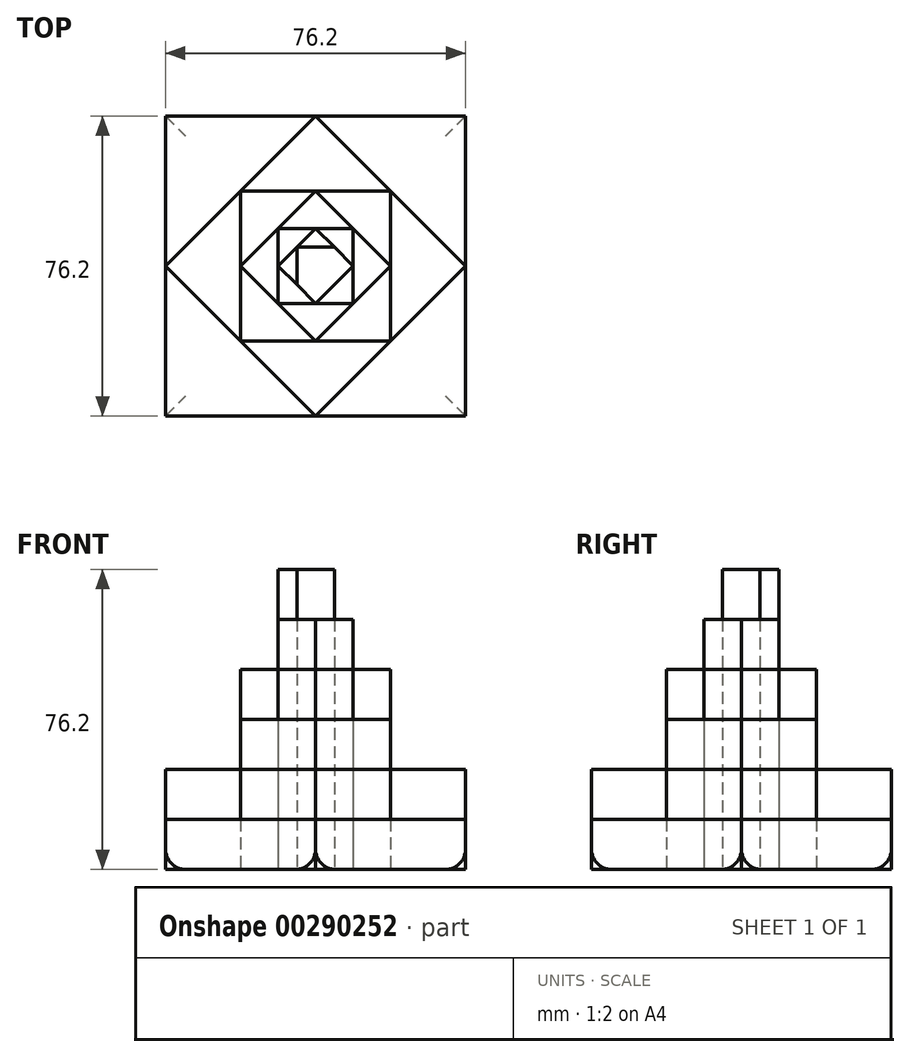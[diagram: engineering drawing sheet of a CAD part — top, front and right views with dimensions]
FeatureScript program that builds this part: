
annotation { "Feature Type Name" : "Feature", "Feature Type Description" : "" }
export const myFeature = defineFeature(function(context is Context, id is Id, definition is map)
    precondition{}
    {
        {
            var Q0;
            Q0=qCreatedBy(makeId("Top.planeOp"),FACE);
            var sketch = newSketch(context, id + "F0", { "sketchPlane" : qUnion([Q0])});
            skPoint(sketch, "E0", {"position": v(0, 0) * mm});
            skLineSegment(sketch, "E1", {"start": v(-38.1, 38.1) * mm, "end": v(-38.1, -38.1) * mm});
            skLineSegment(sketch, "E2", {"start": v(-38.1, -38.1) * mm, "end": v(38.1, -38.1) * mm});
            skLineSegment(sketch, "E3", {"start": v(38.1, -38.1) * mm, "end": v(38.1, 38.1) * mm});
            skLineSegment(sketch, "E4", {"start": v(-38.1, 38.1) * mm, "end": v(38.1, 38.1) * mm});
            skPoint(sketch, "E5", {"position": v(0, -38.1) * mm});
            skPoint(sketch, "E6", {"position": v(38.1, 0) * mm});
            skLineSegment(sketch, "E7", {"start": v(0, 38.1) * mm, "end": v(-38.1, 0) * mm});
            skLineSegment(sketch, "E8", {"start": v(-38.1, 0) * mm, "end": v(0, -38.1) * mm});
            skLineSegment(sketch, "E9", {"start": v(0, 38.1) * mm, "end": v(38.1, 0) * mm});
            skLineSegment(sketch, "E10", {"start": v(38.1, 0) * mm, "end": v(0, -38.1) * mm});
            skLineSegment(sketch, "E11", {"start": v(19.05, 19.05) * mm, "end": v(19.05, -19.05) * mm});
            skLineSegment(sketch, "E12", {"start": v(19.05, -19.05) * mm, "end": v(-19.05, -19.05) * mm});
            skLineSegment(sketch, "E13", {"start": v(-19.05, -19.05) * mm, "end": v(-19.05, 19.05) * mm});
            skLineSegment(sketch, "E14", {"start": v(-19.05, 19.05) * mm, "end": v(19.05, 19.05) * mm});
            skLineSegment(sketch, "E15", {"start": v(0, 19.05) * mm, "end": v(19.05, 0) * mm});
            skLineSegment(sketch, "E16", {"start": v(19.05, 0) * mm, "end": v(0, -19.05) * mm});
            skLineSegment(sketch, "E17", {"start": v(0, -19.05) * mm, "end": v(-19.05, 0) * mm});
            skLineSegment(sketch, "E18", {"start": v(-19.05, 0) * mm, "end": v(0, 19.05) * mm});
            skLineSegment(sketch, "E19", {"start": v(9.52, 9.52) * mm, "end": v(9.52, -9.53) * mm});
            skLineSegment(sketch, "E20", {"start": v(9.52, -9.53) * mm, "end": v(-9.53, -9.53) * mm});
            skLineSegment(sketch, "E21", {"start": v(-9.53, -9.53) * mm, "end": v(-9.53, 9.52) * mm});
            skLineSegment(sketch, "E22", {"start": v(-9.53, 9.52) * mm, "end": v(9.52, 9.52) * mm});
            skLineSegment(sketch, "E23", {"start": v(0, 9.52) * mm, "end": v(-9.53, 0) * mm});
            skLineSegment(sketch, "E24", {"start": v(-9.53, 0) * mm, "end": v(0, -9.53) * mm});
            skLineSegment(sketch, "E25", {"start": v(0, -9.53) * mm, "end": v(9.52, 0) * mm});
            skLineSegment(sketch, "E26", {"start": v(9.52, 0) * mm, "end": v(0, 9.52) * mm});
            skLineSegment(sketch, "E27", {"start": v(-4.76, 4.76) * mm, "end": v(4.76, 4.76) * mm});
            skLineSegment(sketch, "E28", {"start": v(4.76, 4.76) * mm, "end": v(4.76, -4.76) * mm});
            skLineSegment(sketch, "E29", {"start": v(4.76, -4.76) * mm, "end": v(-4.76, -4.76) * mm});
            skLineSegment(sketch, "E30", {"start": v(-4.76, -4.76) * mm, "end": v(-4.76, 4.76) * mm});
            skSolve(sketch);
        }
        {
            var Q0;
            {var subQ0=sQuery(id+"F0.wireOp",EDGE,"E4");var subQ1=sQuery(id+"F0.wireOp",EDGE,"E1");var subQ2=makeQuery(id+"F0.imprint","INTERSECT",VERTEX,{"derivedFrom":[subQ1,subQ0]});Q0=makeQuery(id+"F0.imprint","IMPRINT",FACE,{"disambiguationData":[TD([[makeQuery(id+"F0.imprint","IMPRINT",EDGE,{"disambiguationData":[TD([[subQ2,-1.0]])],"derivedFrom":subQ1}),1.0]])]});}
            var Q1;
            {var subQ0=sQuery(id+"F0.wireOp",EDGE,"E4");var subQ1=sQuery(id+"F0.wireOp",EDGE,"E3");var subQ2=makeQuery(id+"F0.imprint","INTERSECT",VERTEX,{"derivedFrom":[subQ1,subQ0]});Q1=makeQuery(id+"F0.imprint","IMPRINT",FACE,{"disambiguationData":[TD([[makeQuery(id+"F0.imprint","IMPRINT",EDGE,{"disambiguationData":[TD([[subQ2,1.0]])],"derivedFrom":subQ1}),1.0]])]});}
            var Q2;
            {var subQ0=sQuery(id+"F0.wireOp",EDGE,"E3");var subQ1=sQuery(id+"F0.wireOp",EDGE,"E2");var subQ2=makeQuery(id+"F0.imprint","INTERSECT",VERTEX,{"derivedFrom":[subQ1,subQ0]});Q2=makeQuery(id+"F0.imprint","IMPRINT",FACE,{"disambiguationData":[TD([[makeQuery(id+"F0.imprint","IMPRINT",EDGE,{"disambiguationData":[TD([[subQ2,1.0]])],"derivedFrom":subQ1}),1.0]])]});}
            var Q3;
            {var subQ0=sQuery(id+"F0.wireOp",EDGE,"E2");var subQ1=sQuery(id+"F0.wireOp",EDGE,"E1");var subQ2=makeQuery(id+"F0.imprint","INTERSECT",VERTEX,{"derivedFrom":[subQ1,subQ0]});Q3=makeQuery(id+"F0.imprint","IMPRINT",FACE,{"disambiguationData":[TD([[makeQuery(id+"F0.imprint","IMPRINT",EDGE,{"disambiguationData":[TD([[subQ2,1.0]])],"derivedFrom":subQ1}),1.0]])]});}
            extrude(context, id + "F1", {"entities" : qUnion([Q0, Q1, Q2, Q3]), "depth" : 12.7 * mm});
        }
        {
            var Q0;
            {var subQ0=sQuery(id+"F0.wireOp",EDGE,"E8");var subQ1=sQuery(id+"F0.wireOp",EDGE,"E7");var subQ2=makeQuery(id+"F0.imprint","INTERSECT",VERTEX,{"derivedFrom":[sQuery(id+"F0.wireOp",EDGE,"E1"),subQ1,subQ0]});Q0=makeQuery(id+"F0.imprint","IMPRINT",FACE,{"disambiguationData":[TD([[makeQuery(id+"F0.imprint","IMPRINT",EDGE,{"disambiguationData":[TD([[subQ2,1.0]])],"derivedFrom":subQ1}),1.0]])]});}
            var Q1;
            {var subQ0=sQuery(id+"F0.wireOp",EDGE,"E9");var subQ1=sQuery(id+"F0.wireOp",EDGE,"E7");var subQ2=makeQuery(id+"F0.imprint","INTERSECT",VERTEX,{"derivedFrom":[sQuery(id+"F0.wireOp",EDGE,"E4"),subQ1,subQ0]});Q1=makeQuery(id+"F0.imprint","IMPRINT",FACE,{"disambiguationData":[TD([[makeQuery(id+"F0.imprint","IMPRINT",EDGE,{"disambiguationData":[TD([[subQ2,-1.0]])],"derivedFrom":subQ1}),1.0]])]});}
            var Q2;
            {var subQ0=sQuery(id+"F0.wireOp",EDGE,"E10");var subQ1=sQuery(id+"F0.wireOp",EDGE,"E9");var subQ2=makeQuery(id+"F0.imprint","INTERSECT",VERTEX,{"derivedFrom":[sQuery(id+"F0.wireOp",EDGE,"E3"),subQ1,subQ0]});Q2=makeQuery(id+"F0.imprint","IMPRINT",FACE,{"disambiguationData":[TD([[makeQuery(id+"F0.imprint","IMPRINT",EDGE,{"disambiguationData":[TD([[subQ2,1.0]])],"derivedFrom":subQ1}),-1.0]])]});}
            var Q3;
            {var subQ0=sQuery(id+"F0.wireOp",EDGE,"E10");var subQ1=sQuery(id+"F0.wireOp",EDGE,"E8");var subQ2=makeQuery(id+"F0.imprint","INTERSECT",VERTEX,{"derivedFrom":[sQuery(id+"F0.wireOp",EDGE,"E2"),subQ1,subQ0]});Q3=makeQuery(id+"F0.imprint","IMPRINT",FACE,{"disambiguationData":[TD([[makeQuery(id+"F0.imprint","IMPRINT",EDGE,{"disambiguationData":[TD([[subQ2,1.0]])],"derivedFrom":subQ1}),1.0]])]});}
            extrude(context, id + "F2", {"entities" : qUnion([Q0, Q1, Q2, Q3]), "depth" : 25.4 * mm});
        }
        {
            var Q0;
            {var subQ0=sQuery(id+"F0.wireOp",EDGE,"E14");var subQ1=sQuery(id+"F0.wireOp",EDGE,"E13");var subQ2=makeQuery(id+"F0.imprint","INTERSECT",VERTEX,{"derivedFrom":[sQuery(id+"F0.wireOp",EDGE,"E7"),subQ1,subQ0]});Q0=makeQuery(id+"F0.imprint","IMPRINT",FACE,{"disambiguationData":[TD([[makeQuery(id+"F0.imprint","IMPRINT",EDGE,{"disambiguationData":[TD([[subQ2,1.0]])],"derivedFrom":subQ1}),-1.0]])]});}
            var Q1;
            {var subQ0=sQuery(id+"F0.wireOp",EDGE,"E13");var subQ1=sQuery(id+"F0.wireOp",EDGE,"E12");var subQ2=makeQuery(id+"F0.imprint","INTERSECT",VERTEX,{"derivedFrom":[sQuery(id+"F0.wireOp",EDGE,"E8"),subQ1,subQ0]});Q1=makeQuery(id+"F0.imprint","IMPRINT",FACE,{"disambiguationData":[TD([[makeQuery(id+"F0.imprint","IMPRINT",EDGE,{"disambiguationData":[TD([[subQ2,1.0]])],"derivedFrom":subQ1}),-1.0]])]});}
            var Q2;
            {var subQ0=sQuery(id+"F0.wireOp",EDGE,"E12");var subQ1=sQuery(id+"F0.wireOp",EDGE,"E11");var subQ2=makeQuery(id+"F0.imprint","INTERSECT",VERTEX,{"derivedFrom":[sQuery(id+"F0.wireOp",EDGE,"E10"),subQ1,subQ0]});Q2=makeQuery(id+"F0.imprint","IMPRINT",FACE,{"disambiguationData":[TD([[makeQuery(id+"F0.imprint","IMPRINT",EDGE,{"disambiguationData":[TD([[subQ2,1.0]])],"derivedFrom":subQ1}),-1.0]])]});}
            var Q3;
            {var subQ0=sQuery(id+"F0.wireOp",EDGE,"E14");var subQ1=sQuery(id+"F0.wireOp",EDGE,"E11");var subQ2=makeQuery(id+"F0.imprint","INTERSECT",VERTEX,{"derivedFrom":[sQuery(id+"F0.wireOp",EDGE,"E9"),subQ1,subQ0]});Q3=makeQuery(id+"F0.imprint","IMPRINT",FACE,{"disambiguationData":[TD([[makeQuery(id+"F0.imprint","IMPRINT",EDGE,{"disambiguationData":[TD([[subQ2,-1.0]])],"derivedFrom":subQ1}),-1.0]])]});}
            extrude(context, id + "F3", {"entities" : qUnion([Q0, Q1, Q2, Q3]), "depth" : 38.1 * mm});
        }
        {
            var Q0;
            {var subQ3=sQuery(id+"F0.wireOp",EDGE,"E21");Q0=makeQuery(id+"F0.imprint","IMPRINT",FACE,{"disambiguationData":[TD([[makeQuery(id+"F0.imprint","IMPRINT",EDGE,{"derivedFrom":subQ3}),1.0]])]});}
            var Q1;
            {var subQ3=sQuery(id+"F0.wireOp",EDGE,"E20");Q1=makeQuery(id+"F0.imprint","IMPRINT",FACE,{"disambiguationData":[TD([[makeQuery(id+"F0.imprint","IMPRINT",EDGE,{"derivedFrom":subQ3}),1.0]])]});}
            var Q2;
            {var subQ3=sQuery(id+"F0.wireOp",EDGE,"E19");Q2=makeQuery(id+"F0.imprint","IMPRINT",FACE,{"disambiguationData":[TD([[makeQuery(id+"F0.imprint","IMPRINT",EDGE,{"derivedFrom":subQ3}),1.0]])]});}
            var Q3;
            {var subQ3=sQuery(id+"F0.wireOp",EDGE,"E22");Q3=makeQuery(id+"F0.imprint","IMPRINT",FACE,{"disambiguationData":[TD([[makeQuery(id+"F0.imprint","IMPRINT",EDGE,{"derivedFrom":subQ3}),1.0]])]});}
            extrude(context, id + "F4", {"entities" : qUnion([Q0, Q1, Q2, Q3]), "depth" : 50.8 * mm});
        }
        {
            var Q0;
            {var subQ3=sQuery(id+"F0.wireOp",EDGE,"E23");Q0=makeQuery(id+"F0.imprint","IMPRINT",FACE,{"disambiguationData":[TD([[makeQuery(id+"F0.imprint","IMPRINT",EDGE,{"derivedFrom":subQ3}),-1.0]])]});}
            var Q1;
            {var subQ3=sQuery(id+"F0.wireOp",EDGE,"E25");Q1=makeQuery(id+"F0.imprint","IMPRINT",FACE,{"disambiguationData":[TD([[makeQuery(id+"F0.imprint","IMPRINT",EDGE,{"derivedFrom":subQ3}),-1.0]])]});}
            var Q2;
            {var subQ3=sQuery(id+"F0.wireOp",EDGE,"E26");Q2=makeQuery(id+"F0.imprint","IMPRINT",FACE,{"disambiguationData":[TD([[makeQuery(id+"F0.imprint","IMPRINT",EDGE,{"derivedFrom":subQ3}),-1.0]])]});}
            var Q3;
            {var subQ3=sQuery(id+"F0.wireOp",EDGE,"E24");Q3=makeQuery(id+"F0.imprint","IMPRINT",FACE,{"disambiguationData":[TD([[makeQuery(id+"F0.imprint","IMPRINT",EDGE,{"derivedFrom":subQ3}),-1.0]])]});}
            extrude(context, id + "F5", {"entities" : qUnion([Q0, Q1, Q2, Q3]), "depth" : 63.5 * mm});
        }
        {
            var Q0;
            Q0=makeQuery(id+"F0.imprint","IMPRINT",FACE,{"disambiguationData":[TD([[makeQuery(id+"F0.imprint","IMPRINT",EDGE,{"derivedFrom":sQuery(id+"F0.wireOp",EDGE,"E23")}),1.0]])]});
            extrude(context, id + "F6", {"entities" : qUnion([Q0]), "depth" : 76.2 * mm});
        }
        {
            var Q0;
            {var subQ0=sQuery(id+"F0.wireOp",EDGE,"E2");Q0=makeQuery(id+"F1.opExtrude","CAP_EDGE",EDGE,{"disambiguationData":[OSD([subQ0]),TDD([makeQuery(id+"F0.imprint","IMPRINT",EDGE,{"disambiguationData":[TD([[makeQuery(id+"F0.imprint","INTERSECT",VERTEX,{"derivedFrom":[sQuery(id+"F0.wireOp",EDGE,"E1"),subQ0]}),-1.0]])],"derivedFrom":subQ0})])],"isStart":true});}
            var Q1;
            {var subQ0=sQuery(id+"F0.wireOp",EDGE,"E2");Q1=makeQuery(id+"F1.opExtrude","CAP_EDGE",EDGE,{"disambiguationData":[OSD([subQ0]),TDD([makeQuery(id+"F0.imprint","IMPRINT",EDGE,{"disambiguationData":[TD([[makeQuery(id+"F0.imprint","INTERSECT",VERTEX,{"derivedFrom":[subQ0,sQuery(id+"F0.wireOp",EDGE,"E3")]}),1.0]])],"derivedFrom":subQ0})])],"isStart":true});}
            var Q2;
            {var subQ0=sQuery(id+"F0.wireOp",EDGE,"E3");Q2=makeQuery(id+"F1.opExtrude","CAP_EDGE",EDGE,{"disambiguationData":[OSD([subQ0]),TDD([makeQuery(id+"F0.imprint","IMPRINT",EDGE,{"disambiguationData":[TD([[makeQuery(id+"F0.imprint","INTERSECT",VERTEX,{"derivedFrom":[sQuery(id+"F0.wireOp",EDGE,"E2"),subQ0]}),-1.0]])],"derivedFrom":subQ0})])],"isStart":true});}
            var Q3;
            {var subQ0=sQuery(id+"F0.wireOp",EDGE,"E3");Q3=makeQuery(id+"F1.opExtrude","CAP_EDGE",EDGE,{"disambiguationData":[OSD([subQ0]),TDD([makeQuery(id+"F0.imprint","IMPRINT",EDGE,{"disambiguationData":[TD([[makeQuery(id+"F0.imprint","INTERSECT",VERTEX,{"derivedFrom":[subQ0,sQuery(id+"F0.wireOp",EDGE,"E4")]}),1.0]])],"derivedFrom":subQ0})])],"isStart":true});}
            var Q4;
            {var subQ0=sQuery(id+"F0.wireOp",EDGE,"E4");Q4=makeQuery(id+"F1.opExtrude","CAP_EDGE",EDGE,{"disambiguationData":[OSD([subQ0]),TDD([makeQuery(id+"F0.imprint","IMPRINT",EDGE,{"disambiguationData":[TD([[makeQuery(id+"F0.imprint","INTERSECT",VERTEX,{"derivedFrom":[sQuery(id+"F0.wireOp",EDGE,"E3"),subQ0]}),1.0]])],"derivedFrom":subQ0})])],"isStart":true});}
            var Q5;
            {var subQ0=sQuery(id+"F0.wireOp",EDGE,"E4");Q5=makeQuery(id+"F1.opExtrude","CAP_EDGE",EDGE,{"disambiguationData":[OSD([subQ0]),TDD([makeQuery(id+"F0.imprint","IMPRINT",EDGE,{"disambiguationData":[TD([[makeQuery(id+"F0.imprint","INTERSECT",VERTEX,{"derivedFrom":[sQuery(id+"F0.wireOp",EDGE,"E1"),subQ0]}),-1.0]])],"derivedFrom":subQ0})])],"isStart":true});}
            var Q6;
            {var subQ0=sQuery(id+"F0.wireOp",EDGE,"E1");Q6=makeQuery(id+"F1.opExtrude","CAP_EDGE",EDGE,{"disambiguationData":[OSD([subQ0]),TDD([makeQuery(id+"F0.imprint","IMPRINT",EDGE,{"disambiguationData":[TD([[makeQuery(id+"F0.imprint","INTERSECT",VERTEX,{"derivedFrom":[subQ0,sQuery(id+"F0.wireOp",EDGE,"E4")]}),-1.0]])],"derivedFrom":subQ0})])],"isStart":true});}
            var Q7;
            {var subQ0=sQuery(id+"F0.wireOp",EDGE,"E1");Q7=makeQuery(id+"F1.opExtrude","CAP_EDGE",EDGE,{"disambiguationData":[OSD([subQ0]),TDD([makeQuery(id+"F0.imprint","IMPRINT",EDGE,{"disambiguationData":[TD([[makeQuery(id+"F0.imprint","INTERSECT",VERTEX,{"derivedFrom":[subQ0,sQuery(id+"F0.wireOp",EDGE,"E2")]}),1.0]])],"derivedFrom":subQ0})])],"isStart":true});}
            fillet(context, id + "F7", {"entities" : qUnion([Q0, Q1, Q2, Q3, Q4, Q5, Q6, Q7]), "radius" : 5.08 * mm, "tangentPropagation" : true, "allowEdgeOverflow" : false});
        }
    });
